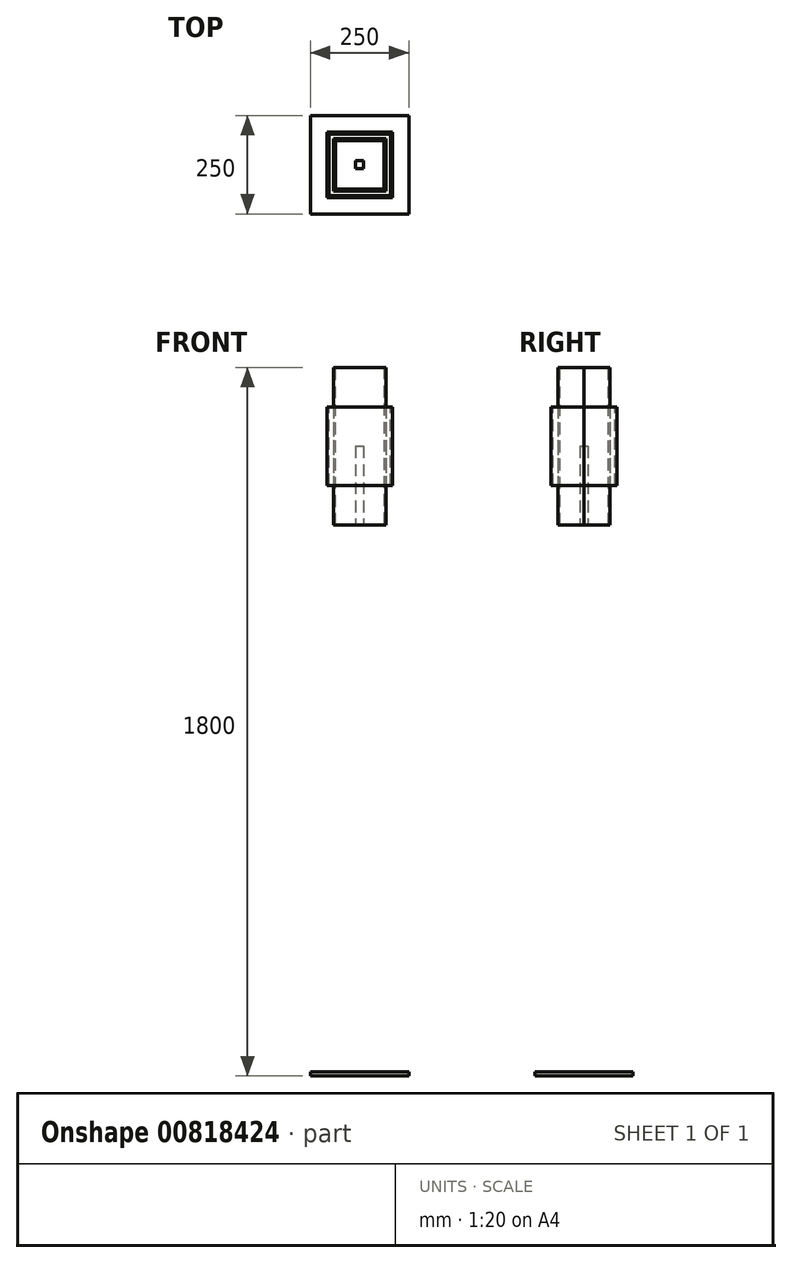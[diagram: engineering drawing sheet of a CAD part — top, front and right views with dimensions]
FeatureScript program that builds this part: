
annotation { "Feature Type Name" : "Feature", "Feature Type Description" : "" }
export const myFeature = defineFeature(function(context is Context, id is Id, definition is map)
    precondition{}
    {
        {
            var Q0;
            Q0=qCreatedBy(makeId("Front.planeOp"),FACE);
            var sketch = newSketch(context, id + "F0", { "sketchPlane" : qUnion([Q0])});
            skLineSegment(sketch, "E0.bottom", {"start": v(-83.3, 1700) * mm, "end": v(83.3, 1700) * mm});
            skLineSegment(sketch, "E0.top", {"start": v(-83.3, 1500) * mm, "end": v(83.3, 1500) * mm});
            skLineSegment(sketch, "E0.left", {"start": v(-83.3, 1700) * mm, "end": v(-83.3, 1500) * mm});
            skLineSegment(sketch, "E0.right", {"start": v(83.3, 1700) * mm, "end": v(83.3, 1500) * mm});
            skLineSegment(sketch, "E1.bottom", {"start": v(-78.3, 1695) * mm, "end": v(78.3, 1695) * mm});
            skLineSegment(sketch, "E1.top", {"start": v(-78.3, 1505) * mm, "end": v(78.3, 1505) * mm});
            skLineSegment(sketch, "E1.left", {"start": v(-78.3, 1695) * mm, "end": v(-78.3, 1505) * mm});
            skLineSegment(sketch, "E1.right", {"start": v(78.3, 1695) * mm, "end": v(78.3, 1505) * mm});
            skLineSegment(sketch, "E2", {"start": v(0, 1700) * mm, "end": v(0, 1695) * mm});
            skLineSegment(sketch, "E3", {"start": v(-78.3, 1600) * mm, "end": v(-83.3, 1600) * mm, "construction": true});
            skPoint(sketch, "E3.endSnap0", {"position": v(-83.3, 1600) * mm});
            skLineSegment(sketch, "E4.bottom", {"start": v(-125, 10) * mm, "end": v(125, 10) * mm});
            skLineSegment(sketch, "E4.top", {"start": v(-125, 0) * mm, "end": v(125, 0) * mm});
            skLineSegment(sketch, "E4.left", {"start": v(-125, 10) * mm, "end": v(-125, 0) * mm});
            skLineSegment(sketch, "E4.right", {"start": v(125, 10) * mm, "end": v(125, 0) * mm});
            skLineSegment(sketch, "E5.bottom", {"start": v(-10, 1600) * mm, "end": v(10, 1600) * mm});
            skLineSegment(sketch, "E5.top", {"start": v(-10, 10) * mm, "end": v(10, 10) * mm});
            skLineSegment(sketch, "E5.left", {"start": v(-10, 1600) * mm, "end": v(-10, 10) * mm});
            skLineSegment(sketch, "E5.right", {"start": v(10, 1600) * mm, "end": v(10, 10) * mm});
            skLineSegment(sketch, "E6", {"start": v(0, 1600) * mm, "end": v(0, 10) * mm, "construction": true});
            skLineSegment(sketch, "E7.bottom", {"start": v(-61.65, 1795) * mm, "end": v(61.65, 1795) * mm});
            skLineSegment(sketch, "E7.top", {"start": v(-61.65, 1405) * mm, "end": v(61.65, 1405) * mm});
            skLineSegment(sketch, "E7.left", {"start": v(-61.65, 1795) * mm, "end": v(-61.65, 1405) * mm});
            skLineSegment(sketch, "E7.right", {"start": v(61.65, 1795) * mm, "end": v(61.65, 1405) * mm});
            skLineSegment(sketch, "E8.bottom", {"start": v(-66.65, 1800) * mm, "end": v(66.65, 1800) * mm});
            skLineSegment(sketch, "E8.top", {"start": v(-66.65, 1400) * mm, "end": v(66.65, 1400) * mm});
            skLineSegment(sketch, "E8.left", {"start": v(-66.65, 1800) * mm, "end": v(-66.65, 1400) * mm});
            skLineSegment(sketch, "E8.right", {"start": v(66.65, 1800) * mm, "end": v(66.65, 1400) * mm});
            skLineSegment(sketch, "E9", {"start": v(0, 1800) * mm, "end": v(0, 1795) * mm, "construction": true});
            skLineSegment(sketch, "E10", {"start": v(-61.65, 1600) * mm, "end": v(-66.65, 1600) * mm, "construction": true});
            skLineSegment(sketch, "E11", {"start": v(0, 1795) * mm, "end": v(0, 1700) * mm, "construction": true});
            skLineSegment(sketch, "E12", {"start": v(0, 1500) * mm, "end": v(0, 1405) * mm, "construction": true});
            skLineSegment(sketch, "E13", {"start": v(-61.65, 1600) * mm, "end": v(61.65, 1600) * mm, "construction": true});
            skLineSegment(sketch, "E14", {"start": v(-61.65, 1405) * mm, "end": v(-61.65, 1400) * mm});
            skLineSegment(sketch, "E15", {"start": v(61.65, 1405) * mm, "end": v(61.65, 1400) * mm});
            skLineSegment(sketch, "E16", {"start": v(-78.3, 1505) * mm, "end": v(-78.3, 1500) * mm});
            skLineSegment(sketch, "E17", {"start": v(78.3, 1505) * mm, "end": v(78.3, 1500) * mm});
            skLineSegment(sketch, "E18", {"start": v(-61.65, 1795) * mm, "end": v(-61.65, 1800) * mm});
            skLineSegment(sketch, "E19", {"start": v(61.65, 1795) * mm, "end": v(61.65, 1800) * mm});
            skLineSegment(sketch, "E20", {"start": v(-78.3, 1695) * mm, "end": v(-78.3, 1700) * mm});
            skLineSegment(sketch, "E21", {"start": v(78.3, 1695) * mm, "end": v(78.3, 1700) * mm});
            skSolve(sketch);
        }
        {
            var Q0;
            Q0=makeQuery(id+"F0.imprint","IMPRINT",FACE,{"disambiguationData":[TD([[makeQuery(id+"F0.imprint","IMPRINT",EDGE,{"derivedFrom":sQuery(id+"F0.wireOp",EDGE,"E4.top")}),1.0]])]});
            extrude(context, id + "F1", {"entities" : qUnion([Q0]), "depth" : 125 * mm, "offsetDistance" : 25 * mm, "hasSecondDirection" : true, "secondDirectionOppositeDirection" : true, "secondDirectionDepth" : 125 * mm});
        }
        {
            var Q0;
            {var subQ0=sQuery(id+"F0.wireOp",EDGE,"E5.top");Q0=makeQuery(id+"F0.imprint","IMPRINT",FACE,{"disambiguationData":[TD([[makeQuery(id+"F0.imprint","IMPRINT",EDGE,{"derivedFrom":subQ0}),1.0]])]});}
            var Q1;
            {var subQ0=sQuery(id+"F0.wireOp",EDGE,"E8.top");var subQ1=sQuery(id+"F0.wireOp",EDGE,"E5.left");var subQ2=makeQuery(id+"F0.imprint","INTERSECT",VERTEX,{"derivedFrom":[subQ1,subQ0]});Q1=makeQuery(id+"F0.imprint","IMPRINT",FACE,{"disambiguationData":[TD([[makeQuery(id+"F0.imprint","IMPRINT",EDGE,{"disambiguationData":[TD([[subQ2,1.0]])],"derivedFrom":subQ1}),1.0]])]});}
            var Q2;
            {var subQ0=sQuery(id+"F0.wireOp",EDGE,"E5.left");var subQ1=sQuery(id+"F0.wireOp",EDGE,"E0.top");var subQ2=makeQuery(id+"F0.imprint","INTERSECT",VERTEX,{"derivedFrom":[subQ1,subQ0]});Q2=makeQuery(id+"F0.imprint","IMPRINT",FACE,{"disambiguationData":[TD([[makeQuery(id+"F0.imprint","IMPRINT",EDGE,{"disambiguationData":[TD([[subQ2,-1.0]])],"derivedFrom":subQ1}),-1.0]])]});}
            var Q3;
            {var subQ0=sQuery(id+"F0.wireOp",EDGE,"E5.left");var subQ1=sQuery(id+"F0.wireOp",EDGE,"E0.top");var subQ2=makeQuery(id+"F0.imprint","INTERSECT",VERTEX,{"derivedFrom":[subQ1,subQ0]});Q3=makeQuery(id+"F0.imprint","IMPRINT",FACE,{"disambiguationData":[TD([[makeQuery(id+"F0.imprint","IMPRINT",EDGE,{"disambiguationData":[TD([[subQ2,-1.0]])],"derivedFrom":subQ1}),1.0]])]});}
            var Q4;
            {var subQ5=sQuery(id+"F0.wireOp",EDGE,"E5.bottom");Q4=makeQuery(id+"F0.imprint","IMPRINT",FACE,{"disambiguationData":[TD([[makeQuery(id+"F0.imprint","IMPRINT",EDGE,{"derivedFrom":subQ5}),-1.0]])]});}
            extrude(context, id + "F2", {"entities" : qUnion([Q0, Q1, Q2, Q3, Q4]), "operationType" : NewBodyOperationType.ADD, "depth" : 10 * mm, "offsetDistance" : 25 * mm, "hasSecondDirection" : true, "secondDirectionOppositeDirection" : true, "secondDirectionDepth" : 10 * mm});
        }
        {
            var Q0;
            {var subQ0=sQuery(id+"F0.wireOp",EDGE,"E0.left");Q0=makeQuery(id+"F0.imprint","IMPRINT",FACE,{"disambiguationData":[TD([[makeQuery(id+"F0.imprint","IMPRINT",EDGE,{"derivedFrom":subQ0}),1.0]])]});}
            var Q1;
            {var subQ0=sQuery(id+"F0.wireOp",EDGE,"E0.right");Q1=makeQuery(id+"F0.imprint","IMPRINT",FACE,{"disambiguationData":[TD([[makeQuery(id+"F0.imprint","IMPRINT",EDGE,{"derivedFrom":subQ0}),-1.0]])]});}
            extrude(context, id + "F3", {"entities" : qUnion([Q0, Q1]), "depth" : 83.3 * mm, "offsetDistance" : 25 * mm});
        }
        {
            var Q0;
            {var subQ0=sQuery(id+"F0.wireOp",EDGE,"E21");Q0=makeQuery(id+"F0.imprint","IMPRINT",FACE,{"disambiguationData":[TD([[makeQuery(id+"F0.imprint","IMPRINT",EDGE,{"derivedFrom":subQ0}),1.0]])]});}
            var Q1;
            {var subQ0=sQuery(id+"F0.wireOp",EDGE,"E2");Q1=makeQuery(id+"F0.imprint","IMPRINT",FACE,{"disambiguationData":[TD([[makeQuery(id+"F0.imprint","IMPRINT",EDGE,{"derivedFrom":subQ0}),1.0]])]});}
            var Q2;
            {var subQ0=sQuery(id+"F0.wireOp",EDGE,"E8.right");var subQ1=sQuery(id+"F0.wireOp",EDGE,"E0.bottom");var subQ2=makeQuery(id+"F0.imprint","INTERSECT",VERTEX,{"derivedFrom":[subQ1,subQ0]});Q2=makeQuery(id+"F0.imprint","IMPRINT",FACE,{"disambiguationData":[TD([[makeQuery(id+"F0.imprint","IMPRINT",EDGE,{"disambiguationData":[TD([[subQ2,1.0]])],"derivedFrom":subQ1}),-1.0]])]});}
            var Q3;
            {var subQ0=sQuery(id+"F0.wireOp",EDGE,"E2");Q3=makeQuery(id+"F0.imprint","IMPRINT",FACE,{"disambiguationData":[TD([[makeQuery(id+"F0.imprint","IMPRINT",EDGE,{"derivedFrom":subQ0}),-1.0]])]});}
            var Q4;
            {var subQ0=sQuery(id+"F0.wireOp",EDGE,"E20");Q4=makeQuery(id+"F0.imprint","IMPRINT",FACE,{"disambiguationData":[TD([[makeQuery(id+"F0.imprint","IMPRINT",EDGE,{"derivedFrom":subQ0}),-1.0]])]});}
            var Q5;
            {var subQ0=sQuery(id+"F0.wireOp",EDGE,"E8.left");var subQ1=sQuery(id+"F0.wireOp",EDGE,"E0.bottom");var subQ2=makeQuery(id+"F0.imprint","INTERSECT",VERTEX,{"derivedFrom":[subQ1,subQ0]});Q5=makeQuery(id+"F0.imprint","IMPRINT",FACE,{"disambiguationData":[TD([[makeQuery(id+"F0.imprint","IMPRINT",EDGE,{"disambiguationData":[TD([[subQ2,-1.0]])],"derivedFrom":subQ1}),-1.0]])]});}
            var Q6;
            {var subQ0=sQuery(id+"F0.wireOp",EDGE,"E1.left");Q6=makeQuery(id+"F0.imprint","IMPRINT",FACE,{"disambiguationData":[TD([[makeQuery(id+"F0.imprint","IMPRINT",EDGE,{"derivedFrom":subQ0}),1.0]])]});}
            var Q7;
            {var subQ0=sQuery(id+"F0.wireOp",EDGE,"E8.left");var subQ1=sQuery(id+"F0.wireOp",EDGE,"E1.bottom");var subQ2=makeQuery(id+"F0.imprint","INTERSECT",VERTEX,{"derivedFrom":[subQ1,subQ0]});Q7=makeQuery(id+"F0.imprint","IMPRINT",FACE,{"disambiguationData":[TD([[makeQuery(id+"F0.imprint","IMPRINT",EDGE,{"disambiguationData":[TD([[subQ2,-1.0]])],"derivedFrom":subQ1}),-1.0]])]});}
            var Q8;
            {var subQ0=sQuery(id+"F0.wireOp",EDGE,"E7.right");var subQ1=sQuery(id+"F0.wireOp",EDGE,"E1.bottom");var subQ2=makeQuery(id+"F0.imprint","INTERSECT",VERTEX,{"derivedFrom":[subQ1,subQ0]});Q8=makeQuery(id+"F0.imprint","IMPRINT",FACE,{"disambiguationData":[TD([[makeQuery(id+"F0.imprint","IMPRINT",EDGE,{"disambiguationData":[TD([[subQ2,-1.0]])],"derivedFrom":subQ1}),-1.0]])]});}
            var Q9;
            {var subQ0=sQuery(id+"F0.wireOp",EDGE,"E1.right");Q9=makeQuery(id+"F0.imprint","IMPRINT",FACE,{"disambiguationData":[TD([[makeQuery(id+"F0.imprint","IMPRINT",EDGE,{"derivedFrom":subQ0}),-1.0]])]});}
            var Q10;
            {var subQ5=sQuery(id+"F0.wireOp",EDGE,"E5.bottom");Q10=makeQuery(id+"F0.imprint","IMPRINT",FACE,{"disambiguationData":[TD([[makeQuery(id+"F0.imprint","IMPRINT",EDGE,{"derivedFrom":subQ5}),1.0]])]});}
            var Q11;
            {var subQ5=sQuery(id+"F0.wireOp",EDGE,"E5.bottom");Q11=makeQuery(id+"F0.imprint","IMPRINT",FACE,{"disambiguationData":[TD([[makeQuery(id+"F0.imprint","IMPRINT",EDGE,{"derivedFrom":subQ5}),-1.0]])]});}
            var Q12;
            {var subQ0=sQuery(id+"F0.wireOp",EDGE,"E17");Q12=makeQuery(id+"F0.imprint","IMPRINT",FACE,{"disambiguationData":[TD([[makeQuery(id+"F0.imprint","IMPRINT",EDGE,{"derivedFrom":subQ0}),-1.0]])]});}
            var Q13;
            {var subQ0=sQuery(id+"F0.wireOp",EDGE,"E8.right");var subQ1=sQuery(id+"F0.wireOp",EDGE,"E0.top");var subQ2=makeQuery(id+"F0.imprint","INTERSECT",VERTEX,{"derivedFrom":[subQ1,subQ0]});Q13=makeQuery(id+"F0.imprint","IMPRINT",FACE,{"disambiguationData":[TD([[makeQuery(id+"F0.imprint","IMPRINT",EDGE,{"disambiguationData":[TD([[subQ2,1.0]])],"derivedFrom":subQ1}),1.0]])]});}
            var Q14;
            {var subQ0=sQuery(id+"F0.wireOp",EDGE,"E5.right");var subQ1=sQuery(id+"F0.wireOp",EDGE,"E0.top");var subQ2=makeQuery(id+"F0.imprint","INTERSECT",VERTEX,{"derivedFrom":[subQ1,subQ0]});Q14=makeQuery(id+"F0.imprint","IMPRINT",FACE,{"disambiguationData":[TD([[makeQuery(id+"F0.imprint","IMPRINT",EDGE,{"disambiguationData":[TD([[subQ2,-1.0]])],"derivedFrom":subQ1}),1.0]])]});}
            var Q15;
            {var subQ0=sQuery(id+"F0.wireOp",EDGE,"E5.left");var subQ1=sQuery(id+"F0.wireOp",EDGE,"E0.top");var subQ2=makeQuery(id+"F0.imprint","INTERSECT",VERTEX,{"derivedFrom":[subQ1,subQ0]});Q15=makeQuery(id+"F0.imprint","IMPRINT",FACE,{"disambiguationData":[TD([[makeQuery(id+"F0.imprint","IMPRINT",EDGE,{"disambiguationData":[TD([[subQ2,-1.0]])],"derivedFrom":subQ1}),1.0]])]});}
            var Q16;
            {var subQ0=sQuery(id+"F0.wireOp",EDGE,"E7.left");var subQ1=sQuery(id+"F0.wireOp",EDGE,"E0.top");var subQ2=makeQuery(id+"F0.imprint","INTERSECT",VERTEX,{"derivedFrom":[subQ1,subQ0]});Q16=makeQuery(id+"F0.imprint","IMPRINT",FACE,{"disambiguationData":[TD([[makeQuery(id+"F0.imprint","IMPRINT",EDGE,{"disambiguationData":[TD([[subQ2,-1.0]])],"derivedFrom":subQ1}),1.0]])]});}
            var Q17;
            {var subQ0=sQuery(id+"F0.wireOp",EDGE,"E8.left");var subQ1=sQuery(id+"F0.wireOp",EDGE,"E0.top");var subQ2=makeQuery(id+"F0.imprint","INTERSECT",VERTEX,{"derivedFrom":[subQ1,subQ0]});Q17=makeQuery(id+"F0.imprint","IMPRINT",FACE,{"disambiguationData":[TD([[makeQuery(id+"F0.imprint","IMPRINT",EDGE,{"disambiguationData":[TD([[subQ2,-1.0]])],"derivedFrom":subQ1}),1.0]])]});}
            var Q18;
            {var subQ0=sQuery(id+"F0.wireOp",EDGE,"E16");Q18=makeQuery(id+"F0.imprint","IMPRINT",FACE,{"disambiguationData":[TD([[makeQuery(id+"F0.imprint","IMPRINT",EDGE,{"derivedFrom":subQ0}),1.0]])]});}
            extrude(context, id + "F4", {"entities" : qUnion([Q0, Q1, Q2, Q3, Q4, Q5, Q6, Q7, Q8, Q9, Q10, Q11, Q12, Q13, Q14, Q15, Q16, Q17, Q18]), "operationType" : NewBodyOperationType.ADD, "depth" : 83.3 * mm, "offsetDistance" : 25 * mm, "hasSecondDirection" : true, "secondDirectionOppositeDirection" : false, "secondDirectionDepth" : 78.3 * mm});
        }
        {
            var Q0;
            {var subQ5=sQuery(id+"F0.wireOp",EDGE,"E19");Q0=makeQuery(id+"F0.imprint","IMPRINT",FACE,{"disambiguationData":[TD([[makeQuery(id+"F0.imprint","IMPRINT",EDGE,{"derivedFrom":subQ5}),-1.0]])]});}
            var Q1;
            {var subQ0=sQuery(id+"F0.wireOp",EDGE,"E8.right");var subQ1=sQuery(id+"F0.wireOp",EDGE,"E0.bottom");var subQ2=makeQuery(id+"F0.imprint","INTERSECT",VERTEX,{"derivedFrom":[subQ1,subQ0]});Q1=makeQuery(id+"F0.imprint","IMPRINT",FACE,{"disambiguationData":[TD([[makeQuery(id+"F0.imprint","IMPRINT",EDGE,{"disambiguationData":[TD([[subQ2,1.0]])],"derivedFrom":subQ1}),-1.0]])]});}
            var Q2;
            {var subQ0=sQuery(id+"F0.wireOp",EDGE,"E7.right");var subQ1=sQuery(id+"F0.wireOp",EDGE,"E1.bottom");var subQ2=makeQuery(id+"F0.imprint","INTERSECT",VERTEX,{"derivedFrom":[subQ1,subQ0]});Q2=makeQuery(id+"F0.imprint","IMPRINT",FACE,{"disambiguationData":[TD([[makeQuery(id+"F0.imprint","IMPRINT",EDGE,{"disambiguationData":[TD([[subQ2,-1.0]])],"derivedFrom":subQ1}),-1.0]])]});}
            var Q3;
            {var subQ0=sQuery(id+"F0.wireOp",EDGE,"E8.right");var subQ1=sQuery(id+"F0.wireOp",EDGE,"E0.top");var subQ2=makeQuery(id+"F0.imprint","INTERSECT",VERTEX,{"derivedFrom":[subQ1,subQ0]});Q3=makeQuery(id+"F0.imprint","IMPRINT",FACE,{"disambiguationData":[TD([[makeQuery(id+"F0.imprint","IMPRINT",EDGE,{"disambiguationData":[TD([[subQ2,1.0]])],"derivedFrom":subQ1}),1.0]])]});}
            var Q4;
            {var subQ5=sQuery(id+"F0.wireOp",EDGE,"E15");Q4=makeQuery(id+"F0.imprint","IMPRINT",FACE,{"disambiguationData":[TD([[makeQuery(id+"F0.imprint","IMPRINT",EDGE,{"derivedFrom":subQ5}),1.0]])]});}
            var Q5;
            {var subQ5=sQuery(id+"F0.wireOp",EDGE,"E14");Q5=makeQuery(id+"F0.imprint","IMPRINT",FACE,{"disambiguationData":[TD([[makeQuery(id+"F0.imprint","IMPRINT",EDGE,{"derivedFrom":subQ5}),-1.0]])]});}
            var Q6;
            {var subQ0=sQuery(id+"F0.wireOp",EDGE,"E8.left");var subQ1=sQuery(id+"F0.wireOp",EDGE,"E0.top");var subQ2=makeQuery(id+"F0.imprint","INTERSECT",VERTEX,{"derivedFrom":[subQ1,subQ0]});Q6=makeQuery(id+"F0.imprint","IMPRINT",FACE,{"disambiguationData":[TD([[makeQuery(id+"F0.imprint","IMPRINT",EDGE,{"disambiguationData":[TD([[subQ2,-1.0]])],"derivedFrom":subQ1}),1.0]])]});}
            var Q7;
            {var subQ0=sQuery(id+"F0.wireOp",EDGE,"E8.left");var subQ1=sQuery(id+"F0.wireOp",EDGE,"E1.bottom");var subQ2=makeQuery(id+"F0.imprint","INTERSECT",VERTEX,{"derivedFrom":[subQ1,subQ0]});Q7=makeQuery(id+"F0.imprint","IMPRINT",FACE,{"disambiguationData":[TD([[makeQuery(id+"F0.imprint","IMPRINT",EDGE,{"disambiguationData":[TD([[subQ2,-1.0]])],"derivedFrom":subQ1}),-1.0]])]});}
            var Q8;
            {var subQ5=sQuery(id+"F0.wireOp",EDGE,"E18");Q8=makeQuery(id+"F0.imprint","IMPRINT",FACE,{"disambiguationData":[TD([[makeQuery(id+"F0.imprint","IMPRINT",EDGE,{"derivedFrom":subQ5}),1.0]])]});}
            var Q9;
            {var subQ0=sQuery(id+"F0.wireOp",EDGE,"E8.left");var subQ1=sQuery(id+"F0.wireOp",EDGE,"E0.bottom");var subQ2=makeQuery(id+"F0.imprint","INTERSECT",VERTEX,{"derivedFrom":[subQ1,subQ0]});Q9=makeQuery(id+"F0.imprint","IMPRINT",FACE,{"disambiguationData":[TD([[makeQuery(id+"F0.imprint","IMPRINT",EDGE,{"disambiguationData":[TD([[subQ2,-1.0]])],"derivedFrom":subQ1}),-1.0]])]});}
            extrude(context, id + "F5", {"entities" : qUnion([Q0, Q1, Q2, Q3, Q4, Q5, Q6, Q7, Q8, Q9]), "depth" : 66.6 * mm, "offsetDistance" : 25 * mm});
        }
        {
            var Q0;
            Q0=makeQuery(id+"F0.imprint","IMPRINT",FACE,{"disambiguationData":[TD([[makeQuery(id+"F0.imprint","IMPRINT",EDGE,{"derivedFrom":sQuery(id+"F0.wireOp",EDGE,"E7.bottom")}),1.0]])]});
            var Q1;
            {var subQ1=sQuery(id+"F0.wireOp",EDGE,"E7.bottom");Q1=makeQuery(id+"F0.imprint","IMPRINT",FACE,{"disambiguationData":[TD([[makeQuery(id+"F0.imprint","IMPRINT",EDGE,{"derivedFrom":subQ1}),-1.0]])]});}
            var Q2;
            {var subQ0=sQuery(id+"F0.wireOp",EDGE,"E2");Q2=makeQuery(id+"F0.imprint","IMPRINT",FACE,{"disambiguationData":[TD([[makeQuery(id+"F0.imprint","IMPRINT",EDGE,{"derivedFrom":subQ0}),1.0]])]});}
            var Q3;
            {var subQ0=sQuery(id+"F0.wireOp",EDGE,"E2");Q3=makeQuery(id+"F0.imprint","IMPRINT",FACE,{"disambiguationData":[TD([[makeQuery(id+"F0.imprint","IMPRINT",EDGE,{"derivedFrom":subQ0}),-1.0]])]});}
            var Q4;
            {var subQ5=sQuery(id+"F0.wireOp",EDGE,"E5.bottom");Q4=makeQuery(id+"F0.imprint","IMPRINT",FACE,{"disambiguationData":[TD([[makeQuery(id+"F0.imprint","IMPRINT",EDGE,{"derivedFrom":subQ5}),1.0]])]});}
            var Q5;
            {var subQ5=sQuery(id+"F0.wireOp",EDGE,"E5.bottom");Q5=makeQuery(id+"F0.imprint","IMPRINT",FACE,{"disambiguationData":[TD([[makeQuery(id+"F0.imprint","IMPRINT",EDGE,{"derivedFrom":subQ5}),-1.0]])]});}
            var Q6;
            {var subQ0=sQuery(id+"F0.wireOp",EDGE,"E5.left");var subQ1=sQuery(id+"F0.wireOp",EDGE,"E0.top");var subQ2=makeQuery(id+"F0.imprint","INTERSECT",VERTEX,{"derivedFrom":[subQ1,subQ0]});Q6=makeQuery(id+"F0.imprint","IMPRINT",FACE,{"disambiguationData":[TD([[makeQuery(id+"F0.imprint","IMPRINT",EDGE,{"disambiguationData":[TD([[subQ2,-1.0]])],"derivedFrom":subQ1}),1.0]])]});}
            var Q7;
            {var subQ0=sQuery(id+"F0.wireOp",EDGE,"E7.left");var subQ1=sQuery(id+"F0.wireOp",EDGE,"E0.top");var subQ2=makeQuery(id+"F0.imprint","INTERSECT",VERTEX,{"derivedFrom":[subQ1,subQ0]});Q7=makeQuery(id+"F0.imprint","IMPRINT",FACE,{"disambiguationData":[TD([[makeQuery(id+"F0.imprint","IMPRINT",EDGE,{"disambiguationData":[TD([[subQ2,-1.0]])],"derivedFrom":subQ1}),1.0]])]});}
            var Q8;
            {var subQ0=sQuery(id+"F0.wireOp",EDGE,"E5.right");var subQ1=sQuery(id+"F0.wireOp",EDGE,"E0.top");var subQ2=makeQuery(id+"F0.imprint","INTERSECT",VERTEX,{"derivedFrom":[subQ1,subQ0]});Q8=makeQuery(id+"F0.imprint","IMPRINT",FACE,{"disambiguationData":[TD([[makeQuery(id+"F0.imprint","IMPRINT",EDGE,{"disambiguationData":[TD([[subQ2,-1.0]])],"derivedFrom":subQ1}),1.0]])]});}
            var Q9;
            {var subQ0=sQuery(id+"F0.wireOp",EDGE,"E5.right");var subQ1=sQuery(id+"F0.wireOp",EDGE,"E0.top");var subQ2=makeQuery(id+"F0.imprint","INTERSECT",VERTEX,{"derivedFrom":[subQ1,subQ0]});Q9=makeQuery(id+"F0.imprint","IMPRINT",FACE,{"disambiguationData":[TD([[makeQuery(id+"F0.imprint","IMPRINT",EDGE,{"disambiguationData":[TD([[subQ2,-1.0]])],"derivedFrom":subQ1}),-1.0]])]});}
            var Q10;
            {var subQ0=sQuery(id+"F0.wireOp",EDGE,"E7.left");var subQ1=sQuery(id+"F0.wireOp",EDGE,"E0.top");var subQ2=makeQuery(id+"F0.imprint","INTERSECT",VERTEX,{"derivedFrom":[subQ1,subQ0]});Q10=makeQuery(id+"F0.imprint","IMPRINT",FACE,{"disambiguationData":[TD([[makeQuery(id+"F0.imprint","IMPRINT",EDGE,{"disambiguationData":[TD([[subQ2,-1.0]])],"derivedFrom":subQ1}),-1.0]])]});}
            var Q11;
            {var subQ0=sQuery(id+"F0.wireOp",EDGE,"E5.left");var subQ1=sQuery(id+"F0.wireOp",EDGE,"E0.top");var subQ2=makeQuery(id+"F0.imprint","INTERSECT",VERTEX,{"derivedFrom":[subQ1,subQ0]});Q11=makeQuery(id+"F0.imprint","IMPRINT",FACE,{"disambiguationData":[TD([[makeQuery(id+"F0.imprint","IMPRINT",EDGE,{"disambiguationData":[TD([[subQ2,-1.0]])],"derivedFrom":subQ1}),-1.0]])]});}
            var Q12;
            {var subQ5=sQuery(id+"F0.wireOp",EDGE,"E15");Q12=makeQuery(id+"F0.imprint","IMPRINT",FACE,{"disambiguationData":[TD([[makeQuery(id+"F0.imprint","IMPRINT",EDGE,{"derivedFrom":subQ5}),-1.0]])]});}
            var Q13;
            {var subQ0=sQuery(id+"F0.wireOp",EDGE,"E8.top");var subQ1=sQuery(id+"F0.wireOp",EDGE,"E5.left");var subQ2=makeQuery(id+"F0.imprint","INTERSECT",VERTEX,{"derivedFrom":[subQ1,subQ0]});Q13=makeQuery(id+"F0.imprint","IMPRINT",FACE,{"disambiguationData":[TD([[makeQuery(id+"F0.imprint","IMPRINT",EDGE,{"disambiguationData":[TD([[subQ2,1.0]])],"derivedFrom":subQ1}),1.0]])]});}
            var Q14;
            {var subQ5=sQuery(id+"F0.wireOp",EDGE,"E14");Q14=makeQuery(id+"F0.imprint","IMPRINT",FACE,{"disambiguationData":[TD([[makeQuery(id+"F0.imprint","IMPRINT",EDGE,{"derivedFrom":subQ5}),1.0]])]});}
            extrude(context, id + "F6", {"entities" : qUnion([Q0, Q1, Q2, Q3, Q4, Q5, Q6, Q7, Q8, Q9, Q10, Q11, Q12, Q13, Q14]), "operationType" : NewBodyOperationType.ADD, "depth" : 66.6 * mm, "offsetDistance" : 25 * mm, "hasSecondDirection" : true, "secondDirectionOppositeDirection" : false, "secondDirectionDepth" : 61.6 * mm});
        }
        {
            var Q0;
            Q0=makeQuery(id+"F5.opExtrude","SWEPT_BODY",BODY,{"disambiguationData":[OSD([sQuery(id+"F0.wireOp",EDGE,"E7.left"),sQuery(id+"F0.wireOp",EDGE,"E8.bottom"),sQuery(id+"F0.wireOp",EDGE,"E8.top"),sQuery(id+"F0.wireOp",EDGE,"E8.left"),sQuery(id+"F0.wireOp",EDGE,"E14"),sQuery(id+"F0.wireOp",EDGE,"E18")])]});
            var Q1;
            Q1=makeQuery(id+"F3.opExtrude","SWEPT_BODY",BODY,{"disambiguationData":[OSD([sQuery(id+"F0.wireOp",EDGE,"E0.bottom"),sQuery(id+"F0.wireOp",EDGE,"E0.top"),sQuery(id+"F0.wireOp",EDGE,"E0.left"),sQuery(id+"F0.wireOp",EDGE,"E1.left"),sQuery(id+"F0.wireOp",EDGE,"E16"),sQuery(id+"F0.wireOp",EDGE,"E20")])]});
            var Q2;
            Q2=qCreatedBy(makeId("Front.planeOp"),FACE);
            mirror(context, id + "F7", {"operationType" : NewBodyOperationType.ADD, "entities" : qUnion([Q0, Q1]), "mirrorPlane" : qUnion([Q2])});
        }
    });
